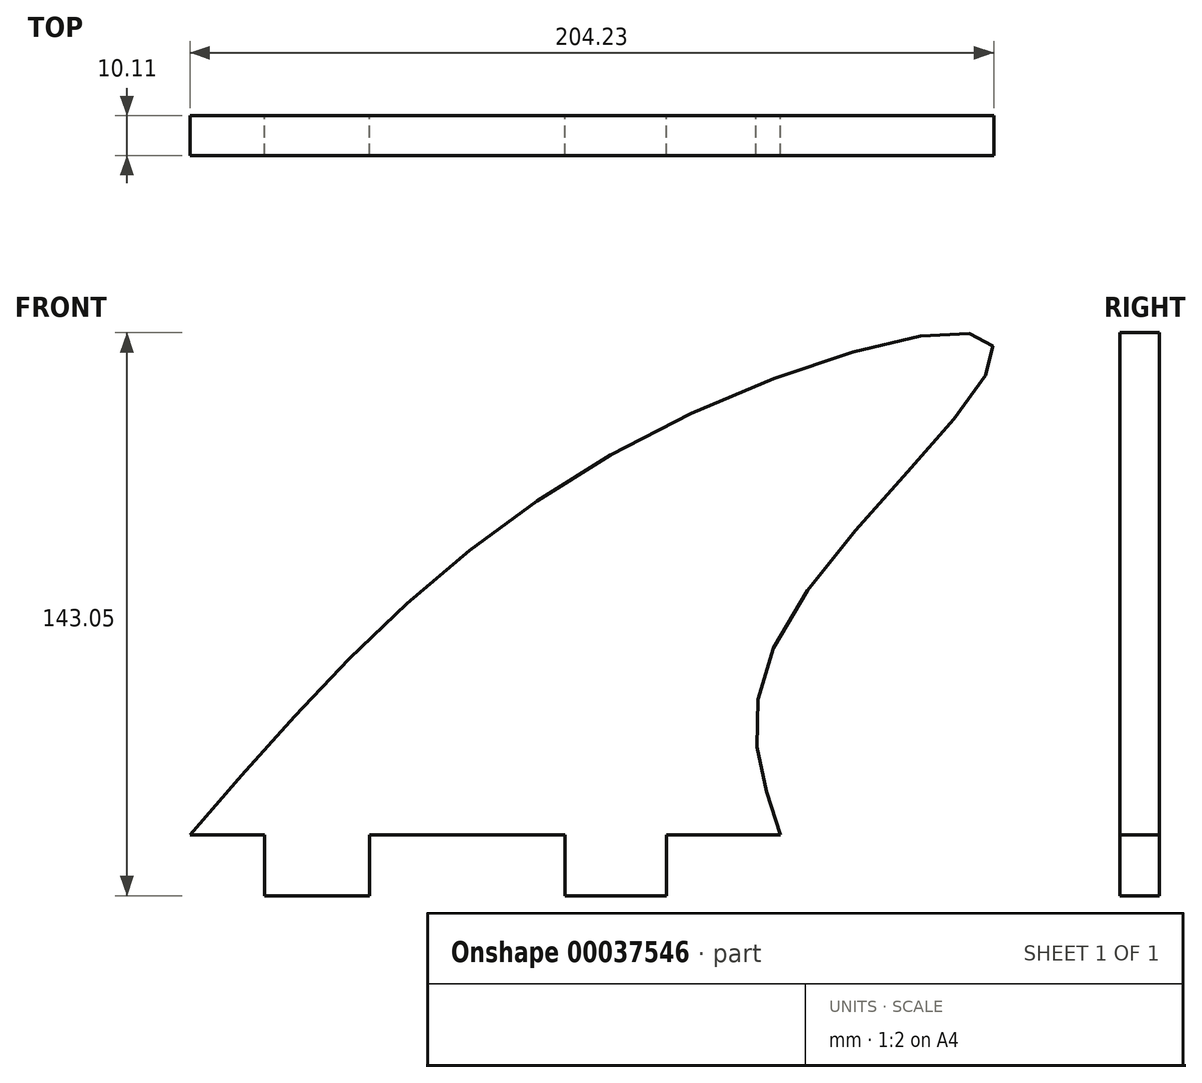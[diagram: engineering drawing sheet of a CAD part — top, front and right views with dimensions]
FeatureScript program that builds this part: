
annotation { "Feature Type Name" : "Feature", "Feature Type Description" : "" }
export const myFeature = defineFeature(function(context is Context, id is Id, definition is map)
    precondition{}
    {
        {
            var Q0;
            Q0=qCreatedBy(makeId("Front.planeOp"),FACE);
            var sketch = newSketch(context, id + "F0", { "sketchPlane" : qUnion([Q0])});
            skLineSegment(sketch, "E0", {"start": v(-76.1, -42.73) * mm, "end": v(-57.18, -42.73) * mm});
            skLineSegment(sketch, "E1", {"start": v(-57.18, -42.73) * mm, "end": v(-57.18, -58.2) * mm});
            skLineSegment(sketch, "E2", {"start": v(-57.18, -58.2) * mm, "end": v(-30.52, -58.2) * mm});
            skLineSegment(sketch, "E3", {"start": v(-30.52, -58.2) * mm, "end": v(-30.52, -42.73) * mm});
            skLineSegment(sketch, "E4", {"start": v(-30.52, -42.73) * mm, "end": v(19.13, -42.73) * mm});
            skLineSegment(sketch, "E5", {"start": v(19.13, -42.73) * mm, "end": v(19.13, -58.2) * mm});
            skLineSegment(sketch, "E6", {"start": v(19.13, -58.2) * mm, "end": v(44.97, -58.2) * mm});
            skLineSegment(sketch, "E7", {"start": v(44.97, -58.2) * mm, "end": v(44.97, -42.73) * mm});
            skLineSegment(sketch, "E8", {"start": v(44.97, -42.73) * mm, "end": v(73.87, -42.73) * mm});
            skFitSpline(sketch, "E9", {"points": [v(73.87, -42.73) * mm, v(73.87, 8.34) * mm, v(128, 81) * mm, v(36.83, 57.18) * mm, v(-76.1, -42.73) * mm], "startDerivative": vector(-86.46, 251.15) * mm, "endDerivative": vector(-301.16, -347.87) * mm});
            skSolve(sketch);
        }
        {
            var Q0;
            Q0=makeQuery(id+"F0.imprint","IMPRINT",FACE,{"disambiguationData":[TD([[makeQuery(id+"F0.imprint","IMPRINT",EDGE,{"derivedFrom":sQuery(id+"F0.wireOp",EDGE,"E0")}),1.0]])]});
            extrude(context, id + "F1", {"entities" : qUnion([Q0]), "depth" : 10.1 * mm});
        }
    });
